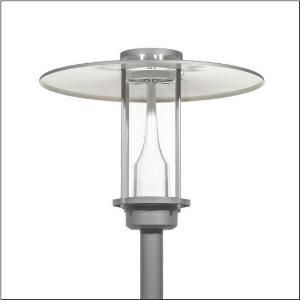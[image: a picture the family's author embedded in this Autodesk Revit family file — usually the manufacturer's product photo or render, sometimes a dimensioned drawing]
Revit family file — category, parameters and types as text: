
# Revit family: city-light_plus_iq___p1_0a_5xa5275bf14hp_a9e6
name_source: partatom
category: Lighting Fixtures
units: mm (PartAtom-declared; Revit-internal decimal feet)

## family parameters
Cut with Voids When Loaded = No
Host = Face
Light Source = No
Part Type = Normal
Room Calculation Point = No
Round Connector Dimension = Use Diameter
Shared = No

## types (1)
- --- (1 x LED, 3710 lm, 33.6 W, 2200K)
    Apparent Load = 34 VA
    CIE Flux Codes = 30 60 90 96 100
    Color Rendering = 70
    Color Temperature = 2200K
    Default Elevation = 1800 mm
    Description = City-Light Plus iQ, mast luminaire, Module 540 iQ-SR, primary light control with 3 zone facetted reflector, of plastic, silver coated, highly specular, structured, primary optical cover: cover, of PMMA, transparent, light distribution: P1.0a, light emission: direct distribution, primary light characteristic: strongly asymmetric, installation type: post-top, LED, High Power LED, rated luminous flux: 3.710lm, luminous efficacy: 110lm/W, light colour: 722, colour temperature: 2200K, control gear: ECG iQ, control: pre-setting: logarithmic dimming characteristic, Street-Remote, Auto-Match, Temp-Guard, Lumen-Switch, Night-Set, Smart-Wire, Light-Fading, Desk-Remote (wireless, voltage-free reading and setting of iQ features in the workshop via application-optimized NFC function/RFID function), optimised constant luminous flux control (CLO 2.0), with terminal, 6-pole, max. 2.5mm², mains connection: 230..240V, AC, 50/60Hz, start of lifetime: 34W, end of service life: 36W, reduction: 15W, luminaire housing, upper part, of glass-fibre reinforced polyester, coated, Siteco® metallic grey (DB 702S), diameter: 750mm, height: 590mm, spigot size: d x l = 76 x 70mm (post-top) | with reducer (optional accessory) 60 x 70mm, post-top mast mounting element, of diecast aluminium, coated, Siteco® metallic grey (DB 702S), Module 540 iQ-SR, traffic white (RAL 9016), equipment: Power, protection rating (complete): IP65, insulation class (complete): insulation class II (safety insulation), certification: CE, ENEC, VDE, packaging unit: 1 piece

Light Distribution: P1.0a
    Height = 590 mm
    Lamp = 1 x LED
    Lamp Light Flux = 3710 lm
    Lamp Power = 33.6 W
    Lamp count = 1
    Length = 750 mm
    Luminous efficacy = 110 lm/W
    Manufacturer = Siteco
    ModVariant = No
    Model = 5XA5275BF14HP
    Number of Poles = 1
    OnlyDefault = Yes
    Power Factor = 1
    Product Name = City-Light Plus iQ | P1.0a
    Product group = mast luminaire | pylon top
    ProductGroupID = 6100
    Protection Class = Protection class II
    Protection Degree = IP 65
    RLX_Detail_Level = 1
    RLX_Emergency_Light_Flux = 0 lm
    RLX_Emergency_Type = 0
    RLX_Emergency_Type_DB = No
    RlxData = <blob elided: 52553 chars, md5=3fec3cad>
    Socket = socket
    Standby Power = 0 W
    System Light Flux = 3710 lm
    System Power = 34 W
    Type Comments = factory setting: luminous flux: 100 % | dim-lin: 254 | 695 mA
    Type Image = l_1006456.jpg
    URL = http://relux.com
    VarID = @adj_166457
    Voltage = 0 V
    Weight = 0.00 kg
    Width = 0 mm  [stored 0 ft]

note: [stored X ft] marks values corroborated as IEEE doubles in the binary element streams (Revit-internal decimal feet)

## geometry (parser evidence)
native form markers: Blend x4, Sweep x10
no freeform markers — native parametric forms only
